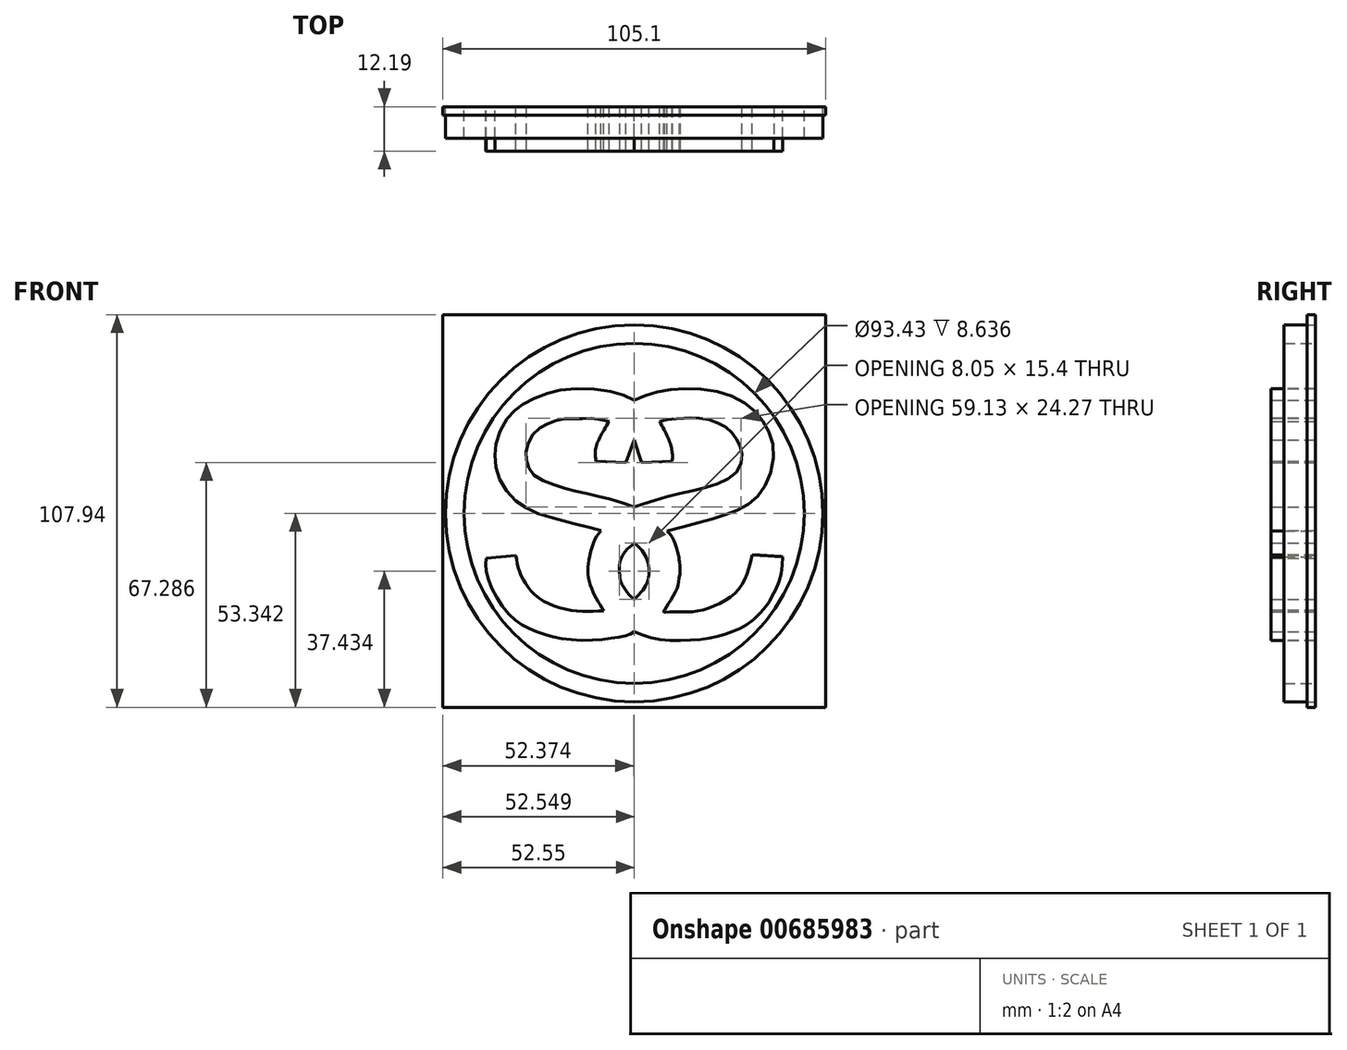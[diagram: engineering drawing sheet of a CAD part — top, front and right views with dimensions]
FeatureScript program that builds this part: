
annotation { "Feature Type Name" : "Feature", "Feature Type Description" : "" }
export const myFeature = defineFeature(function(context is Context, id is Id, definition is map)
    precondition{}
    {
        {
            var Q0;
            Q0=qCreatedBy(makeId("Front.planeOp"),FACE);
            var sketch = newSketch(context, id + "F0", { "sketchPlane" : qUnion([Q0])});
            skCircle(sketch, "E0", {"center": v(0, 3.47) * mm, "radius": 51.82 * mm});
            skCircle(sketch, "E1", {"center": v(0, 3.47) * mm, "radius": 46.71 * mm});
            skSolve(sketch);
        }
        {
            var Q0;
            Q0=qCreatedBy(makeId("Front.planeOp"),FACE);
            var sketch = newSketch(context, id + "F1", { "sketchPlane" : qUnion([Q0])});
            skLineSegment(sketch, "E2", {"start": v(0, 23.6) * mm, "end": v(2, 17.36) * mm});
            skLineSegment(sketch, "E3", {"start": v(2, 17.36) * mm, "end": v(10.45, 17.8) * mm});
            skLineSegment(sketch, "E4", {"start": v(10.45, 17.8) * mm, "end": v(2.27, 17.37) * mm});
            skLineSegment(sketch, "E5", {"start": v(2.27, 17.37) * mm, "end": v(2, 17.36) * mm});
            skLineSegment(sketch, "E6", {"start": v(0, 23.6) * mm, "end": v(-2.26, 17.37) * mm});
            skLineSegment(sketch, "E7", {"start": v(-2.26, 17.37) * mm, "end": v(-10.5, 17.8) * mm});
            skLineSegment(sketch, "E8", {"start": v(-10.5, 17.8) * mm, "end": v(-2.26, 17.37) * mm});
            skFitSpline(sketch, "E9", {"points": [v(10.45, 17.8) * mm, v(10.45, 20.12) * mm, v(9.6, 23.47) * mm, v(6.97, 28.72) * mm], "startDerivative": vector(0.45, 8.6) * mm, "endDerivative": vector(-7.16, 13.08) * mm});
            skFitSpline(sketch, "E10", {"points": [v(6.97, 28.72) * mm, v(9.76, 29.39) * mm, v(13.61, 29.55) * mm, v(15, 29.66) * mm, v(19.14, 29.5) * mm, v(23.1, 28.21) * mm, v(26.17, 26.37) * mm, v(28, 24.03) * mm, v(29.29, 21.3) * mm, v(29.4, 17.33) * mm, v(26.78, 13.6) * mm, v(20.75, 10.86) * mm, v(12.6, 8.9) * mm, v(4.96, 6.84) * mm, v(0, 5.28) * mm], "startDerivative": vector(43.11, 13.77) * mm, "endDerivative": vector(-59.53, -19.27) * mm});
            skFitSpline(sketch, "E11", {"points": [v(-10.5, 17.8) * mm, v(-10.5, 21.58) * mm, v(-6.89, 28.72) * mm], "startDerivative": vector(-1.24, 8.73) * mm, "endDerivative": vector(7.9, 12.86) * mm});
            skFitSpline(sketch, "E12", {"points": [v(-6.89, 28.72) * mm, v(-10.96, 29.5) * mm, v(-15.48, 29.5) * mm, v(-19.61, 29.4) * mm, v(-23.68, 28.11) * mm, v(-27.31, 25.71) * mm, v(-29.65, 21.08) * mm, v(-29.49, 17.8) * mm, v(-27.76, 14.27) * mm, v(-21.73, 11.26) * mm, v(-15.2, 9.36) * mm, v(-8.17, 7.77) * mm, v(0, 5.28) * mm], "startDerivative": vector(-53.38, 13.5) * mm, "endDerivative": vector(77.08, -25.32) * mm});
            skFitSpline(sketch, "E13", {"points": [v(0, -4.74) * mm, v(-2.5, -7.02) * mm, v(-3.94, -10.15) * mm, v(-3.94, -14.11) * mm, v(-3.5, -15.78) * mm, v(-1.37, -18.9) * mm, v(0, -20.14) * mm], "startDerivative": vector(-15, -12.02) * mm, "endDerivative": vector(9.73, -7.3) * mm});
            skFitSpline(sketch, "E14", {"points": [v(0, -4.74) * mm, v(2.27, -6.86) * mm, v(3.7, -9.98) * mm, v(3.98, -13.6) * mm, v(2.81, -17.07) * mm, v(0, -20.14) * mm], "startDerivative": vector(13.19, -10.34) * mm, "endDerivative": vector(-14.61, -13.54) * mm});
            skFitSpline(sketch, "E15", {"points": [v(0, 34.55) * mm, v(5.83, 36.76) * mm, v(13.95, 37.79) * mm, v(24.38, 36.53) * mm, v(32.2, 32.5) * mm, v(36.14, 27.46) * mm, v(38.27, 20.83) * mm, v(36.45, 12.07) * mm, v(32.5, 6.84) * mm, v(26.5, 3.6) * mm, v(19.26, 1.32) * mm, v(9.07, -1.34) * mm], "startDerivative": vector(69.19, 30.3) * mm, "endDerivative": vector(-101.19, -25.79) * mm});
            skFitSpline(sketch, "E16", {"points": [v(9.07, -1.34) * mm, v(10.8, -3.8) * mm, v(11.9, -7.1) * mm, v(12.3, -8.74) * mm, v(12.3, -9.4) * mm, v(12.6, -11.59) * mm, v(12.23, -15.07) * mm, v(11.8, -17.12) * mm, v(9.76, -20.71) * mm, v(8.4, -23.08) * mm], "startDerivative": vector(15.55, -18.37) * mm, "endDerivative": vector(-10.29, -18.69) * mm});
            skFitSpline(sketch, "E17", {"points": [v(8.4, -23.08) * mm, v(8, -23.6) * mm, v(10.45, -23.63) * mm, v(13.45, -23.63) * mm, v(17.16, -23.43) * mm, v(22.45, -21.82) * mm, v(27.5, -18.62) * mm, v(30.52, -14.32) * mm, v(32.35, -8.02) * mm], "startDerivative": vector(-13.55, -11.76) * mm, "endDerivative": vector(9.27, 40.65) * mm});
            skFitSpline(sketch, "E18", {"points": [v(32.35, -8.02) * mm, v(33.84, -8.02) * mm, v(40.82, -8.46) * mm], "startDerivative": vector(3.86, 0.1) * mm, "endDerivative": vector(12.07, -0.88) * mm});
            skFitSpline(sketch, "E19", {"points": [v(40.82, -8.46) * mm, v(40.1, -14.27) * mm, v(37.86, -19.4) * mm, v(36.47, -21.74) * mm, v(31.7, -26.57) * mm, v(27.57, -28.74) * mm, v(22.21, -30.53) * mm, v(15.07, -31.42) * mm, v(6.42, -31.09) * mm, v(0, -29.08) * mm], "startDerivative": vector(-2.14, -52.03) * mm, "endDerivative": vector(-51.11, 20.01) * mm});
            skPoint(sketch, "E20.1.internal.orphan", {"position": v(-0.9, 34.55) * mm});
            skFitSpline(sketch, "E21", {"points": [v(0, 34.55) * mm, v(-3.8, 36.24) * mm, v(-10.45, 37.5) * mm, v(-19.46, 37.5) * mm, v(-24.48, 36.24) * mm, v(-29.83, 33.94) * mm, v(-32.46, 32.01) * mm, v(-34.92, 29.52) * mm, v(-37.6, 24.03) * mm, v(-38.2, 20.09) * mm, v(-37.97, 16.05) * mm, v(-36.28, 11.46) * mm, v(-32.82, 7.2) * mm, v(-28.9, 4.54) * mm, v(-23.53, 2.52) * mm, v(-12.42, -0.36) * mm, v(-9.18, -1.2) * mm], "startDerivative": vector(-64.04, 32.66) * mm, "endDerivative": vector(52.27, -14.06) * mm});
            skFitSpline(sketch, "E22", {"points": [v(-9.18, -1.2) * mm, v(-11.06, -4.3) * mm, v(-12.46, -9.5) * mm, v(-12.66, -12.9) * mm, v(-11.89, -16.77) * mm, v(-10.25, -20.21) * mm, v(-8.41, -23.3) * mm], "startDerivative": vector(-12.5, -17.2) * mm, "endDerivative": vector(11.64, -19.15) * mm});
            skFitSpline(sketch, "E23", {"points": [v(-32.45, -8.17) * mm, v(-31.6, -12.11) * mm, v(-29.26, -16.71) * mm, v(-24, -21.12) * mm, v(-15.66, -23.37) * mm, v(-8.41, -23.3) * mm], "startDerivative": vector(3.94, -24.28) * mm, "endDerivative": vector(32.7, 2.17) * mm});
            skFitSpline(sketch, "E24", {"points": [v(-40.63, -8.9) * mm, v(-32.45, -8.17) * mm], "startDerivative": vector(8.17, 0.73) * mm, "endDerivative": vector(8.17, 0.73) * mm});
            skFitSpline(sketch, "E25", {"points": [v(-40.63, -8.9) * mm, v(-40.63, -12.11) * mm, v(-38.65, -18.08) * mm, v(-33.88, -24.72) * mm, v(-29.62, -27.82) * mm, v(-24.55, -29.89) * mm, v(-18.55, -31.15) * mm, v(-10.1, -31.34) * mm, v(-4.47, -30.59) * mm, v(-1.42, -29.89) * mm, v(0, -29.08) * mm], "startDerivative": vector(-2.9, -37.77) * mm, "endDerivative": vector(22.62, 15.43) * mm});
            skSolve(sketch);
        }
        {
            var Q0;
            Q0 = qSketchRegion(id + "F1", true);
            extrude(context, id + "F2", {"entities" : qUnion([Q0]), "depth" : 12.2 * mm, "offsetDistance" : 25.4 * mm});
        }
        {
            var Q0;
            Q0 = qSketchRegion(id + "F0", true);
            extrude(context, id + "F3", {"entities" : qUnion([Q0]), "depth" : 8.64 * mm, "offsetDistance" : 25.4 * mm});
        }
        {
            var Q0;
            Q0=qCreatedBy(makeId("Front.planeOp"),FACE);
            var sketch = newSketch(context, id + "F4", { "sketchPlane" : qUnion([Q0])});
            skLineSegment(sketch, "E26.bottom", {"start": v(0, -49.87) * mm, "end": v(0, -49.87) * mm});
            skLineSegment(sketch, "E26.top", {"start": v(0, 58.07) * mm, "end": v(0, 58.07) * mm});
            skLineSegment(sketch, "E26.left", {"start": v(0, -49.87) * mm, "end": v(0, 58.07) * mm});
            skLineSegment(sketch, "E26.right", {"start": v(0, -49.87) * mm, "end": v(0, 58.07) * mm});
            skPoint(sketch, "E26.middle", {"position": v(0, 4.1) * mm});
            skLineSegment(sketch, "E27", {"start": v(0, 58.07) * mm, "end": v(-52.55, 58.07) * mm});
            skLineSegment(sketch, "E28", {"start": v(-52.55, 58.07) * mm, "end": v(0, 58.07) * mm});
            skLineSegment(sketch, "E29", {"start": v(0, -49.87) * mm, "end": v(-52.55, -49.87) * mm});
            skLineSegment(sketch, "E30", {"start": v(-52.55, -49.87) * mm, "end": v(-52.55, 58.07) * mm});
            skLineSegment(sketch, "E31", {"start": v(0, 58.07) * mm, "end": v(52.55, 58.07) * mm});
            skLineSegment(sketch, "E32", {"start": v(52.55, 58.07) * mm, "end": v(0, 58.07) * mm});
            skLineSegment(sketch, "E33", {"start": v(0, -49.87) * mm, "end": v(52.55, -49.87) * mm});
            skLineSegment(sketch, "E34", {"start": v(52.55, -49.87) * mm, "end": v(52.55, 58.07) * mm});
            skSolve(sketch);
        }
        {
            var Q0;
            Q0 = qSketchRegion(id + "F4", true);
            extrude(context, id + "F5", {"entities" : qUnion([Q0]), "depth" : 2.3 * mm, "offsetDistance" : 25.4 * mm});
        }
    });
